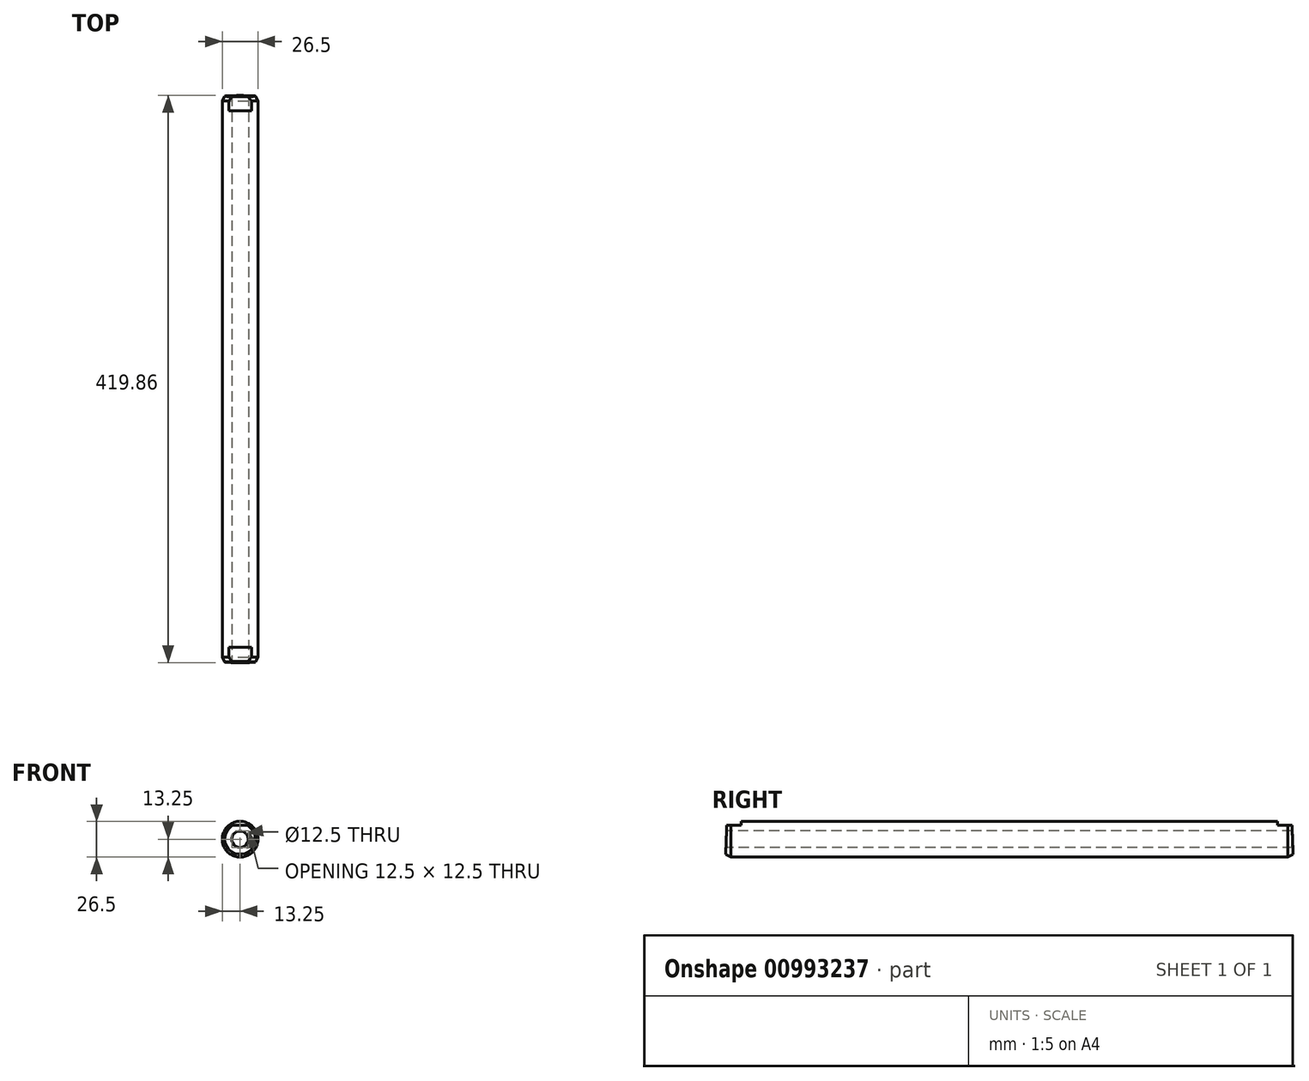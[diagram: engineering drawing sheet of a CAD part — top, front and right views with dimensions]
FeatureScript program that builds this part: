
annotation { "Feature Type Name" : "Feature", "Feature Type Description" : "" }
export const myFeature = defineFeature(function(context is Context, id is Id, definition is map)
    precondition{}
    {
        {
            var Q0;
            Q0=qCreatedBy(makeId("Front.planeOp"),FACE);
            var sketch = newSketch(context, id + "F0", { "sketchPlane" : qUnion([Q0])});
            skCircle(sketch, "E0", {"center": v(0, 0) * mm, "radius": 13.25 * mm});
            skSolve(sketch);
        }
        {
            var Q0;
            Q0 = qSketchRegion(id + "F0", true);
            extrude(context, id + "F1", {"entities" : qUnion([Q0]), "depth" : (420 / 2) * mm, "offsetDistance" : 25 * mm});
        }
        {
            var Q0;
            Q0=makeQuery(id+"F1.opExtrude","CAP_FACE",FACE,{"disambiguationData":[OSD([sQuery(id+"F0.wireOp",EDGE,"E0")])],"isStart":false});
            var sketch = newSketch(context, id + "F2", { "sketchPlane" : qUnion([Q0])});
            skLineSegment(sketch, "E1", {"start": v(-8.4, 10.25) * mm, "end": v(8.4, 10.25) * mm});
            skArc(sketch, "E2", {"start": v(8.4, 10.25) * mm, "mid": v(0, 13.25) * mm, "end": v(-8.4, 10.25) * mm});
            skSolve(sketch);
        }
        {
            var Q0;
            Q0 = qSketchRegion(id + "F2", true);
            extrude(context, id + "F3", {"entities" : qUnion([Q0]), "operationType" : NewBodyOperationType.REMOVE, "oppositeDirection" : true, "depth" : 11.5 * mm, "offsetDistance" : 25 * mm});
        }
        {
            var Q0;
            Q0=makeQuery(id+"F1.opExtrude","CAP_FACE",FACE,{"disambiguationData":[OSD([sQuery(id+"F0.wireOp",EDGE,"E0")])],"isStart":false});
            var sketch = newSketch(context, id + "F4", { "sketchPlane" : qUnion([Q0])});
            skCircle(sketch, "E3", {"center": v(0, 0) * mm, "radius": 6.25 * mm});
            skSolve(sketch);
        }
        {
            var Q0;
            Q0 = qSketchRegion(id + "F4", true);
            extrude(context, id + "F5", {"entities" : qUnion([Q0]), "operationType" : NewBodyOperationType.REMOVE, "endBound" : BoundingType.THROUGH_ALL, "oppositeDirection" : true, "depth" : 25 * mm, "offsetDistance" : 25 * mm});
        }
        {
            var Q0;
            Q0=qCreatedBy(makeId("Right.planeOp"),FACE);
            var sketch = newSketch(context, id + "F6", { "sketchPlane" : qUnion([Q0])});
            skLineSegment(sketch, "E4", {"start": v(0, 0) * mm, "end": v(-210, 0) * mm, "construction": true});
            skLineSegment(sketch, "E5", {"start": v(-206, -13.25) * mm, "end": v(-210, -11.25) * mm});
            skLineSegment(sketch, "E6", {"start": v(-210, -11.25) * mm, "end": v(-210, -15.62) * mm});
            skLineSegment(sketch, "E7", {"start": v(-210, -15.62) * mm, "end": v(-206, -13.25) * mm});
            skSolve(sketch);
        }
        {
            var Q0;
            Q0 = qSketchRegion(id + "F6", true);
            var Q1;
            Q1=sQuery(id+"F6.wireOp",EDGE,"E4");
            revolve(context, id + "F7", {"operationType" : NewBodyOperationType.REMOVE, "surfaceOperationType" : NewSurfaceOperationType.NEW, "entities" : qUnion([Q0]), "axis" : qUnion([Q1]), "revolveType" : RevolveType.FULL, "oppositeDirection" : true});
        }
        {
            var Q0;
            Q0=qCreatedBy(makeId("Right.planeOp"),FACE);
            var sketch = newSketch(context, id + "F8", { "sketchPlane" : qUnion([Q0])});
            skLineSegment(sketch, "E8", {"start": v(-210, 13.25) * mm, "end": v(-210, -13.25) * mm});
            skLineSegment(sketch, "E9", {"start": v(-210, 13.25) * mm, "end": v(-209, 13.25) * mm});
            skLineSegment(sketch, "E10", {"start": v(-209, 13.25) * mm, "end": v(-210, -13.25) * mm});
            skSolve(sketch);
        }
        {
            var Q0;
            Q0 = qSketchRegion(id + "F8", true);
            extrude(context, id + "F9", {"entities" : qUnion([Q0]), "operationType" : NewBodyOperationType.REMOVE, "endBound" : BoundingType.THROUGH_ALL, "oppositeDirection" : true, "depth" : 25 * mm, "offsetDistance" : 25 * mm, "hasSecondDirection" : true, "secondDirectionBound" : SecondDirectionBoundingType.THROUGH_ALL, "secondDirectionOppositeDirection" : false, "secondDirectionDepth" : 25 * mm});
        }
        {
            var Q0;
            Q0=makeQuery(id+"F1.opExtrude","SWEPT_BODY",BODY,{"disambiguationData":[OSD([sQuery(id+"F0.wireOp",EDGE,"E0")])]});
            var Q1;
            Q1=qCreatedBy(makeId("Front.planeOp"),FACE);
            mirror(context, id + "F10", {"operationType" : NewBodyOperationType.ADD, "entities" : qUnion([Q0]), "mirrorPlane" : qUnion([Q1])});
        }
    });
